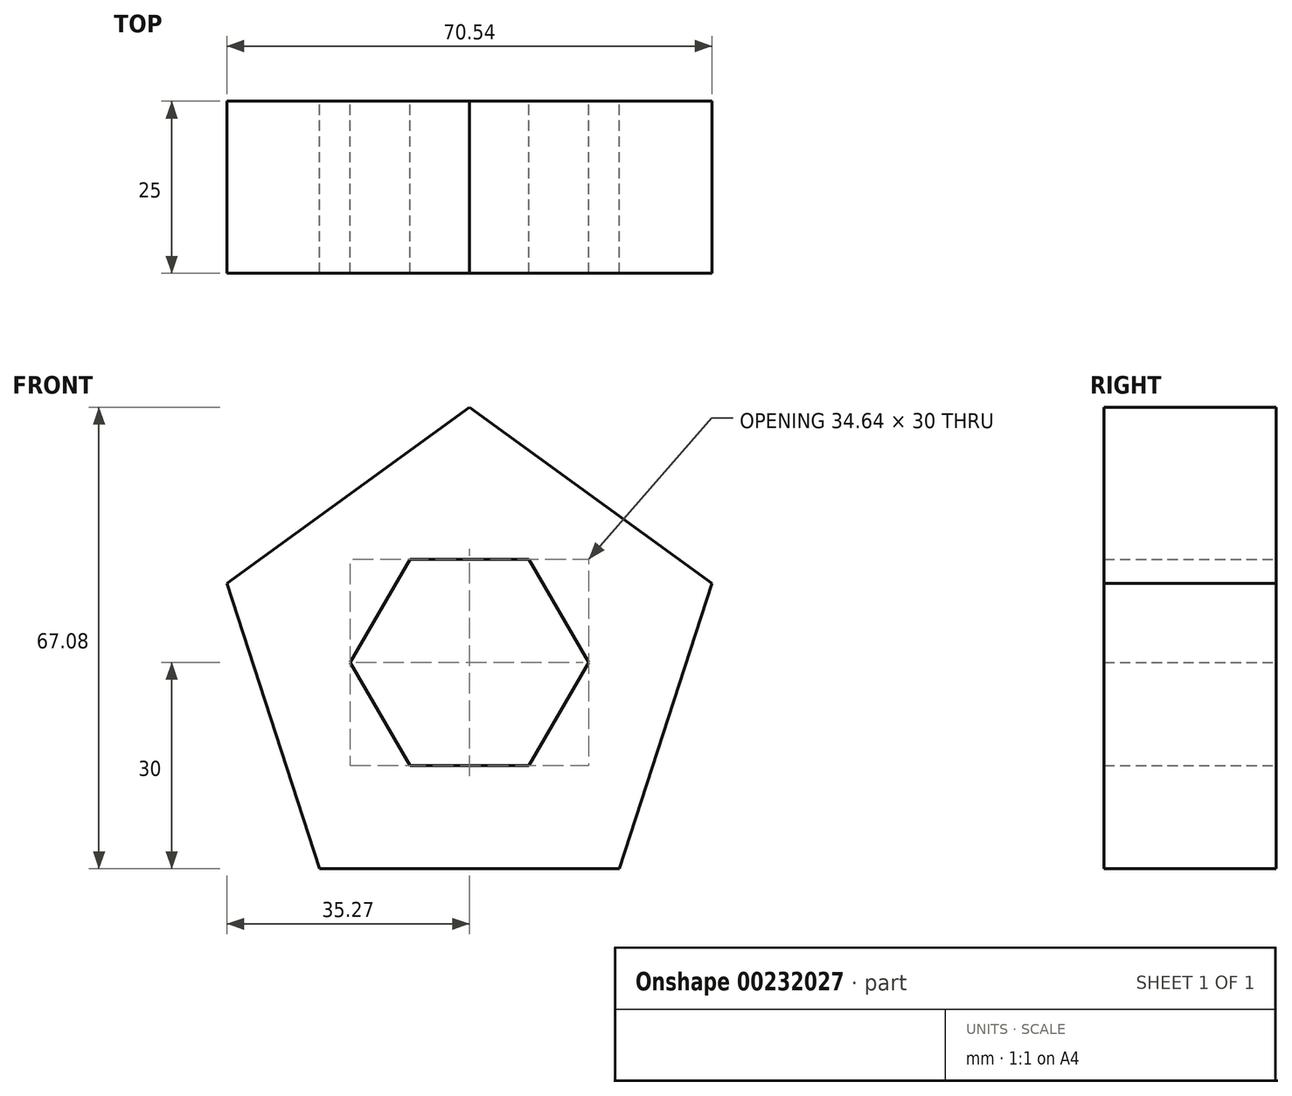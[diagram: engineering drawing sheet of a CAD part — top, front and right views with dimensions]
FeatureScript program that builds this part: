
annotation { "Feature Type Name" : "Feature", "Feature Type Description" : "" }
export const myFeature = defineFeature(function(context is Context, id is Id, definition is map)
    precondition{}
    {
        {
            var Q0;
            Q0=qCreatedBy(makeId("Front.planeOp"),FACE);
            var sketch = newSketch(context, id + "F0", { "sketchPlane" : qUnion([Q0])});
            skCircle(sketch, "E0.cCircle", {"center": v(0, 0) * mm, "radius": 30 * mm, "construction": true});
            skLineSegment(sketch, "E0.0", {"start": v(-35.27, 11.46) * mm, "end": v(0, 37.08) * mm});
            skLineSegment(sketch, "E0.1", {"start": v(0, 37.08) * mm, "end": v(35.27, 11.46) * mm});
            skLineSegment(sketch, "E0.2", {"start": v(35.27, 11.46) * mm, "end": v(21.8, -30) * mm});
            skLineSegment(sketch, "E0.3", {"start": v(21.8, -30) * mm, "end": v(-21.8, -30) * mm});
            skLineSegment(sketch, "E0.4", {"start": v(-21.8, -30) * mm, "end": v(-35.27, 11.46) * mm});
            skPoint(sketch, "E0.0.midPoint", {"position": v(-17.63, 24.27) * mm});
            skCircle(sketch, "E1.cCircle", {"center": v(0, 0) * mm, "radius": 15 * mm, "construction": true});
            skLineSegment(sketch, "E1.0", {"start": v(-8.66, 15) * mm, "end": v(8.66, 15) * mm});
            skLineSegment(sketch, "E1.1", {"start": v(8.66, 15) * mm, "end": v(17.32, 0) * mm});
            skLineSegment(sketch, "E1.2", {"start": v(17.32, 0) * mm, "end": v(8.66, -15) * mm});
            skLineSegment(sketch, "E1.3", {"start": v(8.66, -15) * mm, "end": v(-8.66, -15) * mm});
            skLineSegment(sketch, "E1.4", {"start": v(-8.66, -15) * mm, "end": v(-17.32, 0) * mm});
            skLineSegment(sketch, "E1.5", {"start": v(-17.32, 0) * mm, "end": v(-8.66, 15) * mm});
            skPoint(sketch, "E1.0.midPoint", {"position": v(0, 15) * mm});
            skSolve(sketch);
        }
        {
            var Q0;
            Q0 = qSketchRegion(id + "F0", true);
            extrude(context, id + "F1", {"entities" : qUnion([Q0]), "depth" : 25 * mm});
        }
    });
